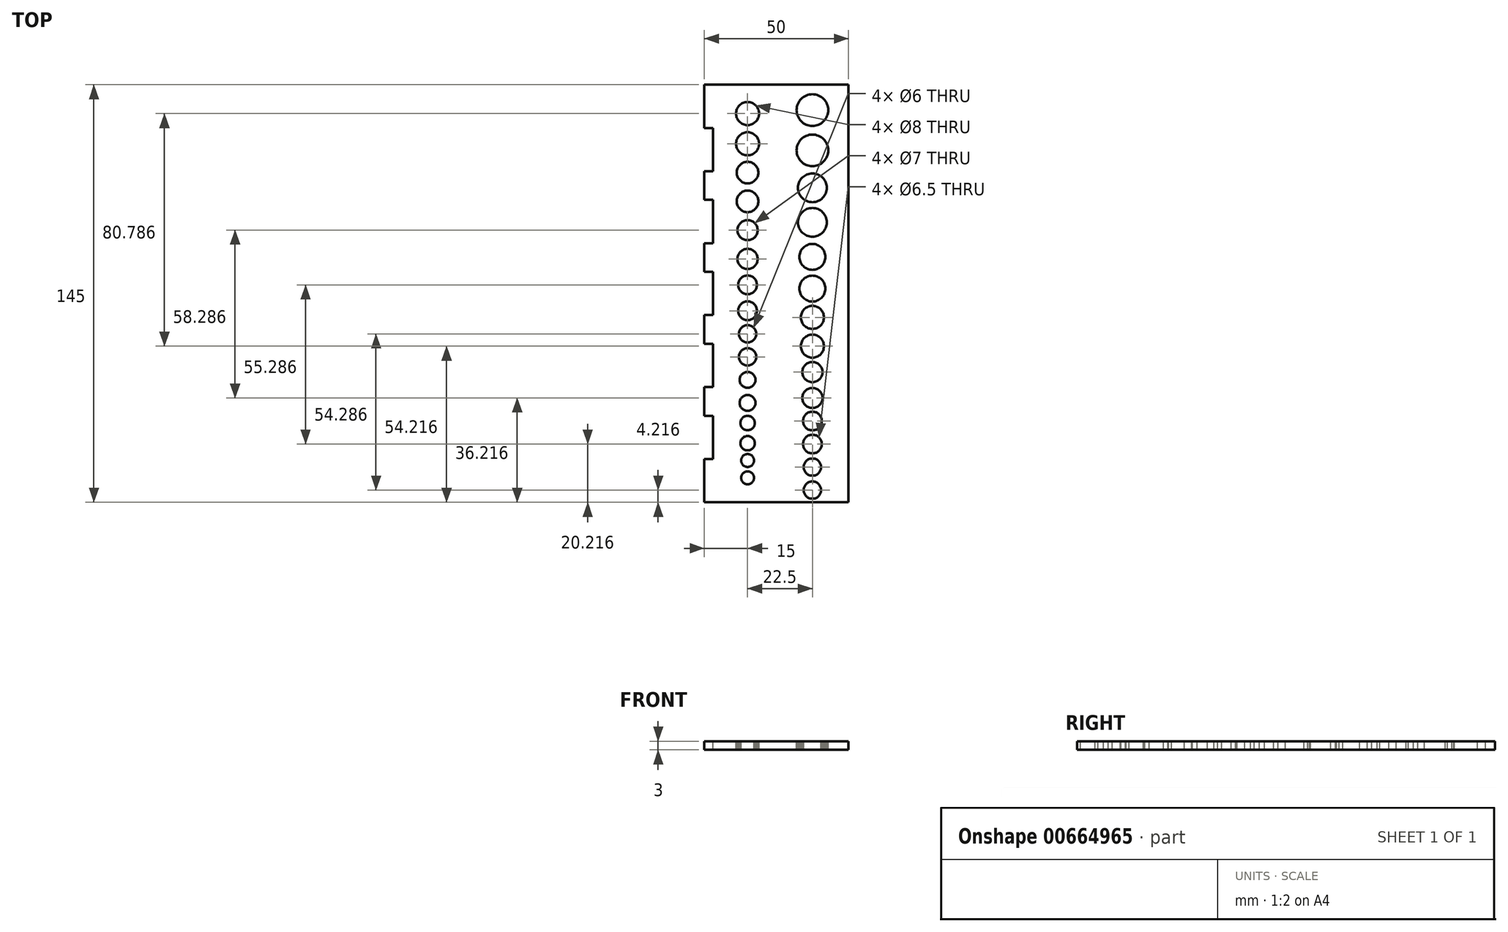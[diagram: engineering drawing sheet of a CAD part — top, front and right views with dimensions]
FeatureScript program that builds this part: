
annotation { "Feature Type Name" : "Feature", "Feature Type Description" : "" }
export const myFeature = defineFeature(function(context is Context, id is Id, definition is map)
    precondition{}
    {
        {
            var Q0;
            Q0=qCreatedBy(makeId("Right.planeOp"),FACE);
            var sketch = newSketch(context, id + "F0", { "sketchPlane" : qUnion([Q0])});
            skLineSegment(sketch, "E0.bottom", {"start": v(-32.27, 18.55) * mm, "end": v(113.95, 18.55) * mm});
            skLineSegment(sketch, "E0.top", {"start": v(-32.27, 13.9) * mm, "end": v(113.95, 13.9) * mm});
            skLineSegment(sketch, "E0.left", {"start": v(-32.27, 18.55) * mm, "end": v(-32.27, 13.9) * mm});
            skLineSegment(sketch, "E0.right", {"start": v(113.95, 18.55) * mm, "end": v(113.95, 13.9) * mm});
            skLineSegment(sketch, "E1.bottom", {"start": v(-32.27, 13.9) * mm, "end": v(-26.87, 13.9) * mm});
            skLineSegment(sketch, "E1.top", {"start": v(-32.27, -7.89) * mm, "end": v(-26.87, -7.89) * mm});
            skLineSegment(sketch, "E1.left", {"start": v(-32.27, 13.9) * mm, "end": v(-32.27, -7.89) * mm});
            skLineSegment(sketch, "E1.right", {"start": v(-26.87, 13.9) * mm, "end": v(-26.87, -7.89) * mm});
            skLineSegment(sketch, "E2.bottom", {"start": v(113.95, 13.9) * mm, "end": v(107.51, 13.9) * mm});
            skLineSegment(sketch, "E2.top", {"start": v(113.95, -47.04) * mm, "end": v(107.51, -47.04) * mm});
            skLineSegment(sketch, "E2.left", {"start": v(113.95, 13.9) * mm, "end": v(113.95, -47.04) * mm});
            skLineSegment(sketch, "E2.right", {"start": v(107.51, 13.9) * mm, "end": v(107.51, -47.04) * mm});
            skLineSegment(sketch, "E3", {"start": v(-32.27, 50.78) * mm, "end": v(113.95, 50.78) * mm, "construction": true});
            skSolve(sketch);
        }
        {
            var Q0;
            {var subQ0=sQuery(id+"F0.wireOp",EDGE,"E1.bottom");Q0=makeQuery(id+"F0.imprint","IMPRINT",FACE,{"disambiguationData":[TD([[makeQuery(id+"F0.imprint","IMPRINT",EDGE,{"derivedFrom":subQ0}),-1.0]])]});}
            var Q1;
            Q1=makeQuery(id+"F0.imprint","IMPRINT",FACE,{"disambiguationData":[TD([[makeQuery(id+"F0.imprint","IMPRINT",EDGE,{"derivedFrom":sQuery(id+"F0.wireOp",EDGE,"E0.bottom")}),-1.0]])]});
            var Q2;
            {var subQ0=sQuery(id+"F0.wireOp",EDGE,"E2.bottom");Q2=makeQuery(id+"F0.imprint","IMPRINT",FACE,{"disambiguationData":[TD([[makeQuery(id+"F0.imprint","IMPRINT",EDGE,{"derivedFrom":subQ0}),1.0]])]});}
            var Q3;
            {var subQ5=sQuery(id+"F0.wireOp",EDGE,"E1.top");Q3=makeQuery(id+"F0.imprint","IMPRINT",FACE,{"disambiguationData":[TD([[makeQuery(id+"F0.imprint","IMPRINT",EDGE,{"derivedFrom":subQ5}),-1.0]])]});}
            var Q4;
            {var subQ0=sQuery(id+"F0.wireOp",EDGE,"E2.top");Q4=makeQuery(id+"F0.imprint","IMPRINT",FACE,{"disambiguationData":[TD([[makeQuery(id+"F0.imprint","IMPRINT",EDGE,{"derivedFrom":subQ0}),-1.0]])]});}
            var Q5;
            {var subQ0=sQuery(id+"F0.wireOp",EDGE,"E1.top");Q5=makeQuery(id+"F0.imprint","IMPRINT",FACE,{"disambiguationData":[TD([[makeQuery(id+"F0.imprint","IMPRINT",EDGE,{"derivedFrom":subQ0}),1.0]])]});}
            extrude(context, id + "F1", {"entities" : qUnion([Q0, Q1, Q2, Q3, Q4, Q5]), "endBound" : BoundingType.SYMMETRIC, "depth" : 25 * mm, "offsetDistance" : 25 * mm});
        }
        {
            var Q0;
            Q0=makeQuery(id+"F1.opExtrude","SWEPT_FACE",FACE,{"disambiguationData":[OSD([sQuery(id+"F0.wireOp",EDGE,"E0.bottom")])]});
            var sketch = newSketch(context, id + "F2", { "sketchPlane" : qUnion([Q0])});
            skCircle(sketch, "E4", {"center": v(0, -28.05) * mm, "radius": 3 * mm});
            skCircle(sketch, "E5", {"center": v(0, -20.05) * mm, "radius": 3 * mm});
            skCircle(sketch, "E6", {"center": v(0, -12.05) * mm, "radius": 3.25 * mm});
            skCircle(sketch, "E7", {"center": v(0, -4.05) * mm, "radius": 3.25 * mm});
            skCircle(sketch, "E8", {"center": v(0, 3.95) * mm, "radius": 3.5 * mm});
            skCircle(sketch, "E9", {"center": v(0, 12.95) * mm, "radius": 3.5 * mm});
            skCircle(sketch, "E10", {"center": v(0, 21.95) * mm, "radius": 4 * mm});
            skCircle(sketch, "E11", {"center": v(0, 31.95) * mm, "radius": 4 * mm});
            skCircle(sketch, "E12", {"center": v(0, 41.95) * mm, "radius": 4.5 * mm});
            skCircle(sketch, "E13", {"center": v(0, 52.95) * mm, "radius": 4.5 * mm});
            skCircle(sketch, "E14", {"center": v(0, 64.95) * mm, "radius": 5 * mm});
            skCircle(sketch, "E15", {"center": v(0, 76.95) * mm, "radius": 5 * mm});
            skCircle(sketch, "E16", {"center": v(0, 89.95) * mm, "radius": 5.5 * mm});
            skCircle(sketch, "E17", {"center": v(0, 103.95) * mm, "radius": 5.5 * mm});
            skSolve(sketch);
        }
        {
            var Q0;
            Q0=qSketchRegion(id+"F2",true);
            extrude(context, id + "F3", {"entities" : qUnion([Q0]), "operationType" : NewBodyOperationType.REMOVE, "endBound" : BoundingType.UP_TO_NEXT, "oppositeDirection" : true, "depth" : 25 * mm, "offsetDistance" : 25 * mm});
        }
        {
            var Q0;
            Q0=makeQuery(id+"F1.opExtrude","SWEPT_FACE",FACE,{"disambiguationData":[OSD([sQuery(id+"F0.wireOp",EDGE,"E0.right"),sQuery(id+"F0.wireOp",EDGE,"E2.left")])]});
            var sketch = newSketch(context, id + "F4", { "sketchPlane" : qUnion([Q0])});
            skLineSegment(sketch, "E18.bottom", {"start": v(12.5, -47.04) * mm, "end": v(-12.5, -47.04) * mm});
            skLineSegment(sketch, "E18.top", {"start": v(12.5, 15.55) * mm, "end": v(-12.5, 15.55) * mm});
            skLineSegment(sketch, "E18.left", {"start": v(12.5, -47.04) * mm, "end": v(12.5, 15.55) * mm});
            skLineSegment(sketch, "E18.right", {"start": v(-12.5, -47.04) * mm, "end": v(-12.5, 15.55) * mm});
            skSolve(sketch);
        }
        {
            var Q0;
            Q0 = qSketchRegion(id + "F4", true);
            var Q1;
            Q1=makeQuery(id+"F1.opExtrude","SWEPT_FACE",FACE,{"disambiguationData":[OSD([sQuery(id+"F0.wireOp",EDGE,"E0.left"),sQuery(id+"F0.wireOp",EDGE,"E1.left")])]});
            extrude(context, id + "F5", {"entities" : qUnion([Q0]), "operationType" : NewBodyOperationType.REMOVE, "endBound" : BoundingType.UP_TO_SURFACE, "oppositeDirection" : true, "depth" : 25 * mm, "endBoundEntityFace" : qUnion([Q1]), "offsetDistance" : 25 * mm});
        }
        {
            var Q0;
            Q0=makeQuery(id+"F1.opExtrude","CAP_FACE",FACE,{"disambiguationData":[OSD([sQuery(id+"F0.wireOp",EDGE,"E0.bottom"),sQuery(id+"F0.wireOp",EDGE,"E0.top"),sQuery(id+"F0.wireOp",EDGE,"E0.left"),sQuery(id+"F0.wireOp",EDGE,"E0.right"),sQuery(id+"F0.wireOp",EDGE,"E1.top"),sQuery(id+"F0.wireOp",EDGE,"E1.left"),sQuery(id+"F0.wireOp",EDGE,"E1.right"),sQuery(id+"F0.wireOp",EDGE,"E2.top"),sQuery(id+"F0.wireOp",EDGE,"E2.left"),sQuery(id+"F0.wireOp",EDGE,"E2.right")])],"isStart":true});
            extrude(context, id + "F6", {"entities" : qUnion([Q0]), "operationType" : NewBodyOperationType.ADD, "depth" : 25 * mm, "offsetDistance" : 25 * mm});
        }
        {
            var Q0;
            {var subQ0=sQuery(id+"F0.wireOp",EDGE,"E0.bottom");Q0=makeQuery(id+"F6.boolean.opBoolean","MERGE",FACE,{"derivedFrom":[makeQuery(id+"F1.opExtrude","SWEPT_FACE",FACE,{"disambiguationData":[OSD([subQ0])]}),makeQuery(id+"F6.opExtrude","SWEPT_FACE",FACE,{"disambiguationData":[OSD([subQ0])]})]});}
            var sketch = newSketch(context, id + "F7", { "sketchPlane" : qUnion([Q0])});
            skLineSegment(sketch, "E19.bottom", {"start": v(-37.5, -17.27) * mm, "end": v(-34.5, -17.27) * mm});
            skLineSegment(sketch, "E19.top", {"start": v(-37.5, -2.27) * mm, "end": v(-34.5, -2.27) * mm});
            skLineSegment(sketch, "E19.left", {"start": v(-37.5, -17.27) * mm, "end": v(-37.5, -2.27) * mm});
            skLineSegment(sketch, "E19.right", {"start": v(-34.5, -17.27) * mm, "end": v(-34.5, -2.27) * mm});
            skLineSegment(sketch, "E20.0.1.0", {"start": v(-37.5, 22.73) * mm, "end": v(-34.5, 22.73) * mm});
            skLineSegment(sketch, "E20.0.1.1", {"start": v(-37.5, 7.73) * mm, "end": v(-34.5, 7.73) * mm});
            skLineSegment(sketch, "E20.0.1.2", {"start": v(-37.5, 7.73) * mm, "end": v(-37.5, 22.73) * mm});
            skLineSegment(sketch, "E20.0.1.3", {"start": v(-34.5, 7.73) * mm, "end": v(-34.5, 22.73) * mm});
            skLineSegment(sketch, "E20.0.2.0", {"start": v(-37.5, 47.73) * mm, "end": v(-34.5, 47.73) * mm});
            skLineSegment(sketch, "E20.0.2.1", {"start": v(-37.5, 32.73) * mm, "end": v(-34.5, 32.73) * mm});
            skLineSegment(sketch, "E20.0.2.2", {"start": v(-37.5, 32.73) * mm, "end": v(-37.5, 47.73) * mm});
            skLineSegment(sketch, "E20.0.2.3", {"start": v(-34.5, 32.73) * mm, "end": v(-34.5, 47.73) * mm});
            skLineSegment(sketch, "E20.0.3.0", {"start": v(-37.5, 72.73) * mm, "end": v(-34.5, 72.73) * mm});
            skLineSegment(sketch, "E20.0.3.1", {"start": v(-37.5, 57.73) * mm, "end": v(-34.5, 57.73) * mm});
            skLineSegment(sketch, "E20.0.3.2", {"start": v(-37.5, 57.73) * mm, "end": v(-37.5, 72.73) * mm});
            skLineSegment(sketch, "E20.0.3.3", {"start": v(-34.5, 57.73) * mm, "end": v(-34.5, 72.73) * mm});
            skLineSegment(sketch, "E20.0.4.0", {"start": v(-37.5, 97.73) * mm, "end": v(-34.5, 97.73) * mm});
            skLineSegment(sketch, "E20.0.4.1", {"start": v(-37.5, 82.73) * mm, "end": v(-34.5, 82.73) * mm});
            skLineSegment(sketch, "E20.0.4.2", {"start": v(-37.5, 82.73) * mm, "end": v(-37.5, 97.73) * mm});
            skLineSegment(sketch, "E20.0.4.3", {"start": v(-34.5, 82.73) * mm, "end": v(-34.5, 97.73) * mm});
            skLineSegment(sketch, "E20.direction1", {"start": v(-37.5, -17.27) * mm, "end": v(-12.5, -17.27) * mm, "construction": true});
            skLineSegment(sketch, "E20.direction2", {"start": v(-37.5, -17.27) * mm, "end": v(-37.5, 7.73) * mm, "construction": true});
            skLineSegment(sketch, "E21.bottom", {"start": v(-37.5, 113.95) * mm, "end": v(12.5, 113.95) * mm});
            skLineSegment(sketch, "E21.top", {"start": v(-37.5, 112.73) * mm, "end": v(12.5, 112.73) * mm});
            skLineSegment(sketch, "E21.left", {"start": v(-37.5, 113.95) * mm, "end": v(-37.5, 112.73) * mm});
            skLineSegment(sketch, "E21.right", {"start": v(12.5, 113.95) * mm, "end": v(12.5, 112.73) * mm});
            skSolve(sketch);
        }
        {
            var Q0;
            Q0 = qSketchRegion(id + "F7", true);
            extrude(context, id + "F8", {"entities" : qUnion([Q0]), "operationType" : NewBodyOperationType.REMOVE, "endBound" : BoundingType.UP_TO_NEXT, "oppositeDirection" : true, "depth" : 25 * mm, "offsetDistance" : 25 * mm});
        }
        {
            var Q0;
            {var subQ0=sQuery(id+"F0.wireOp",EDGE,"E0.bottom");Q0=makeQuery(id+"F6.boolean.opBoolean","MERGE",FACE,{"derivedFrom":[makeQuery(id+"F1.opExtrude","SWEPT_FACE",FACE,{"disambiguationData":[OSD([subQ0])]}),makeQuery(id+"F6.opExtrude","SWEPT_FACE",FACE,{"disambiguationData":[OSD([subQ0])]})]});}
            var sketch = newSketch(context, id + "F9", { "sketchPlane" : qUnion([Q0])});
            skCircle(sketch, "E22", {"center": v(-22.5, 102.73) * mm, "radius": 4 * mm});
            skCircle(sketch, "E23", {"center": v(-22.5, 92.23) * mm, "radius": 4 * mm});
            skCircle(sketch, "E24", {"center": v(-22.5, 82.23) * mm, "radius": 3.75 * mm});
            skCircle(sketch, "E25", {"center": v(-22.5, 72.23) * mm, "radius": 3.75 * mm});
            skCircle(sketch, "E26", {"center": v(-22.5, 62.23) * mm, "radius": 3.5 * mm});
            skCircle(sketch, "E27", {"center": v(-22.5, 52.23) * mm, "radius": 3.5 * mm});
            skCircle(sketch, "E28", {"center": v(-22.5, 43.23) * mm, "radius": 3.25 * mm});
            skCircle(sketch, "E29", {"center": v(-22.5, 34.23) * mm, "radius": 3.25 * mm});
            skCircle(sketch, "E30", {"center": v(-22.5, 26.23) * mm, "radius": 3 * mm});
            skCircle(sketch, "E31", {"center": v(-22.5, 18.23) * mm, "radius": 3 * mm});
            skCircle(sketch, "E32", {"center": v(-22.5, 10.23) * mm, "radius": 2.75 * mm});
            skCircle(sketch, "E33", {"center": v(-22.5, 2.23) * mm, "radius": 2.75 * mm});
            skCircle(sketch, "E34", {"center": v(-22.5, -4.77) * mm, "radius": 2.5 * mm});
            skCircle(sketch, "E35", {"center": v(-22.5, -11.77) * mm, "radius": 2.5 * mm});
            skCircle(sketch, "E36", {"center": v(-22.5, -17.77) * mm, "radius": 2.25 * mm});
            skCircle(sketch, "E37", {"center": v(-22.5, -23.77) * mm, "radius": 2.25 * mm});
            skSolve(sketch);
        }
        {
            var Q0;
            Q0 = qSketchRegion(id + "F9", true);
            extrude(context, id + "F10", {"entities" : qUnion([Q0]), "operationType" : NewBodyOperationType.REMOVE, "endBound" : BoundingType.UP_TO_NEXT, "oppositeDirection" : true, "depth" : 25 * mm, "offsetDistance" : 25 * mm});
        }
    });
